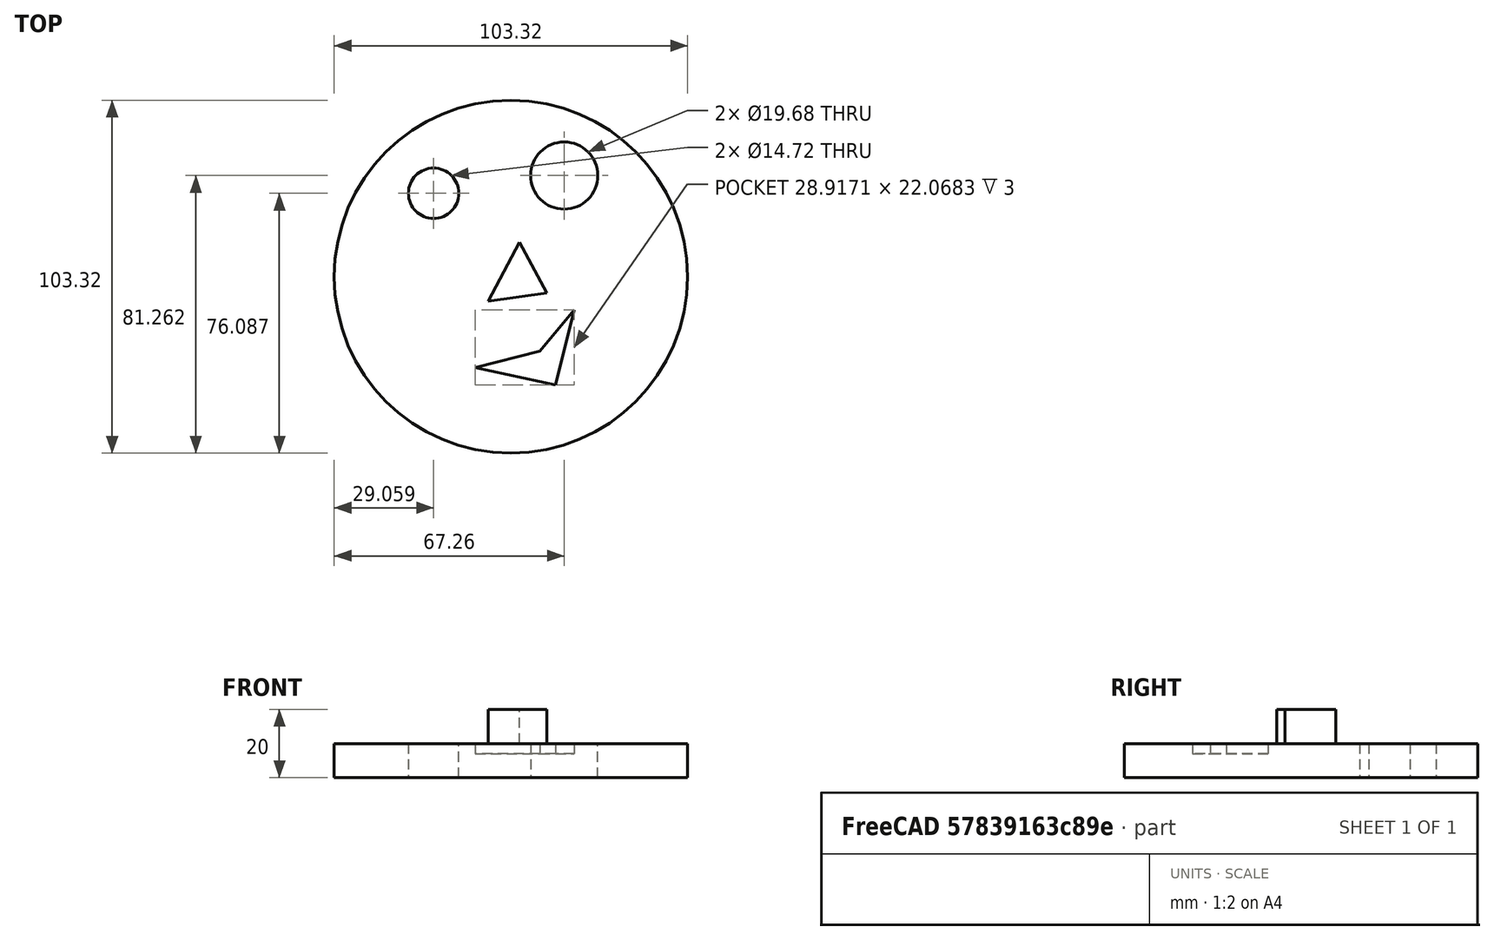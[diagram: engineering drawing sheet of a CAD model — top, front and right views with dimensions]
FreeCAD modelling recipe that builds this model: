
FCSTD DOCUMENT  (FreeCAD 0.16R6707 (Git))
Label: 02-diseno-libre-cara
License: All rights reserved
LicenseURL: http://en.wikipedia.org/wiki/All_rights_reserved
objects: Sketcher::SketchObject×3, PartDesign::Pad×2, PartDesign::Pocket×1
note: 9 computed .brp shape members not serialized (recipe doc carries the construction recipe); baked Part::Feature solids carry a one-line shape summary decoded from their .brp

FEATURE [Sketcher::SketchObject] Sketch
  sketch-geometry (3):
    g0: Circle CenterX=0 CenterY=0 CenterZ=0 NormalX=0 NormalY=0 NormalZ=1 Radius=51.6618
    g1: Circle CenterX=-22.601 CenterY=24.4273 CenterZ=0 NormalX=0 NormalY=0 NormalZ=1 Radius=7.36222
    g2: Circle CenterX=15.6 CenterY=29.602 CenterZ=0 NormalX=0 NormalY=0 NormalZ=1 Radius=9.83751
  constraints (1):
    c: Coincident(g0,g-1)
FEATURE [PartDesign::Pad] Pad
  Length = 10
  Length2 = 100
  Sketch = -> Sketch
  Type = 0
FEATURE [Sketcher::SketchObject] Sketch001
  Placement = pos=(0,0,10) rot=(0,0,1;0rad)
  Support = -> Pad [Face5]
  sketch-geometry (4):
    g0: LineSegment StartX=-10.4254 StartY=-26.5581 StartZ=0 EndX=8.44684 EndY=-21.84 EndZ=0
    g1: LineSegment StartX=8.44684 StartY=-21.84 StartZ=0 EndX=18.4917 EndY=-9.66439 EndZ=0
    g2: LineSegment StartX=18.4917 StartY=-9.66439 StartZ=0 EndX=13.0127 EndY=-31.7327 EndZ=0
    g3: LineSegment StartX=13.0127 StartY=-31.7327 StartZ=0 EndX=-10.4254 EndY=-26.5581 EndZ=0
  constraints (4):
    c: Coincident(g0,g1)
    c: Coincident(g1,g2)
    c: Coincident(g2,g3)
    c: Coincident(g3,g0)
FEATURE [PartDesign::Pocket] Pocket
  Length = 3
  Sketch = -> Sketch001
  Type = 0
FEATURE [Sketcher::SketchObject] Sketch002
  Placement = pos=(0,0,10) rot=(0,0,1;0rad)
  Support = -> Pocket [Face3]
  sketch-geometry (3):
    g0: LineSegment StartX=-6.59915 StartY=-7.15683 StartZ=0 EndX=2.50954 EndY=10.1311 EndZ=0
    g1: LineSegment StartX=2.50954 StartY=10.1311 StartZ=0 EndX=10.5029 EndY=-4.74023 EndZ=0
    g2: LineSegment StartX=-6.59915 StartY=-7.15683 StartZ=0 EndX=10.5029 EndY=-4.74023 EndZ=0
  constraints (3):
    c: Coincident(g0,g1)
    c: Coincident(g2,g0)
    c: Coincident(g2,g1)
FEATURE [PartDesign::Pad] Pad001
  Length = 10
  Length2 = 100
  Sketch = -> Sketch002
  Type = 0
